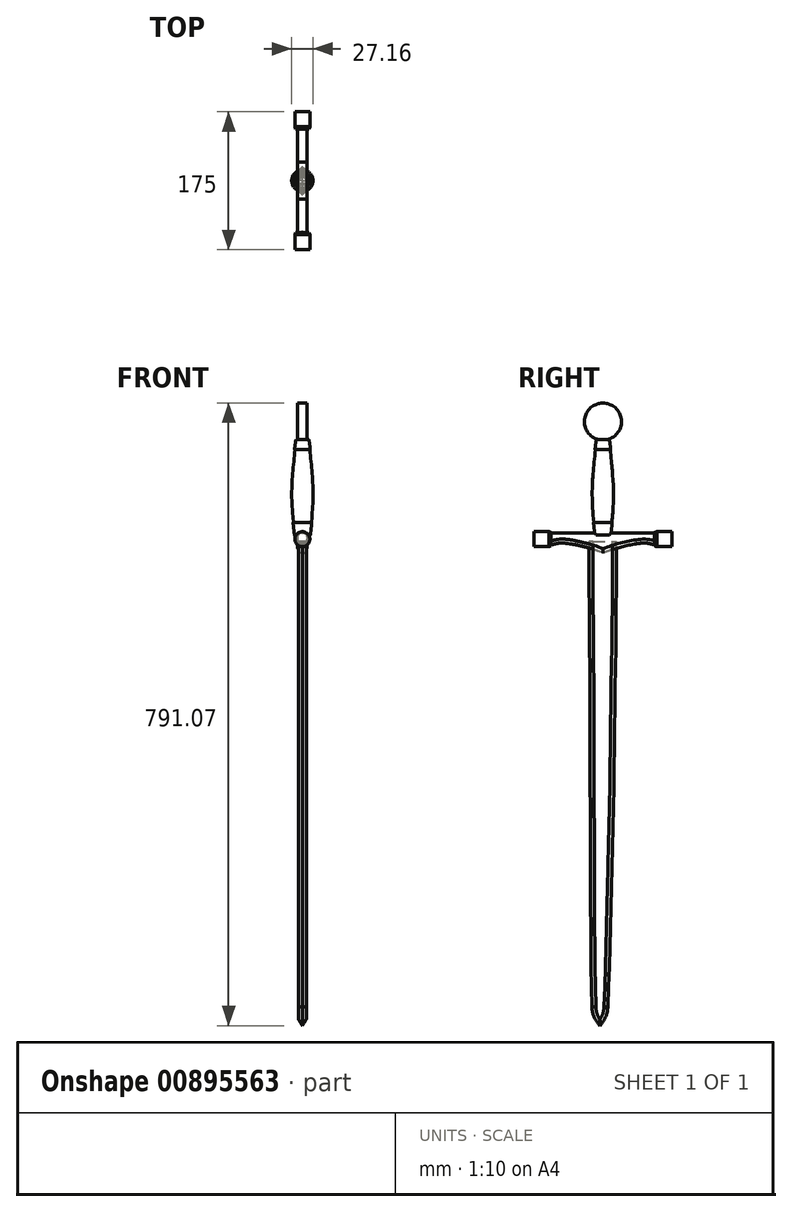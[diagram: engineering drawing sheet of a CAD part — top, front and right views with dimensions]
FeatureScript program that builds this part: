
annotation { "Feature Type Name" : "Feature", "Feature Type Description" : "" }
export const myFeature = defineFeature(function(context is Context, id is Id, definition is map)
    precondition{}
    {
        {
            var Q0;
            Q0=qCreatedBy(makeId("Right.planeOp"),FACE);
            var sketch = newSketch(context, id + "F0", { "sketchPlane" : qUnion([Q0])});
            skFitSpline(sketch, "E0", {"points": [v(15.7, 316.85) * mm, v(15.44, 255.83) * mm, v(14.96, 183.2) * mm, v(13.55, 114.23) * mm, v(12.35, 11.96) * mm, v(11.01, -48.46) * mm, v(9.54, -115.03) * mm, v(7.8, -186.55) * mm, v(6.57, -230.05) * mm, v(4.54, -274.5) * mm], "startDerivative": vector(8.51, -507.05) * mm, "endDerivative": vector(-24.21, -488.92) * mm});
            skFitSpline(sketch, "E1", {"points": [v(4.54, -274.5) * mm, v(-5.59, -298.39) * mm], "startDerivative": vector(0.63, -32.82) * mm, "endDerivative": vector(-13.34, -16.01) * mm});
            skFitSpline(sketch, "E2.MirrorCS", {"points": [v(-18.98, 316.87) * mm, v(-19.04, 251.48) * mm, v(-18.4, 181.8) * mm, v(-18.09, 112.43) * mm, v(-17.8, 12.24) * mm, v(-17.58, -48.2) * mm, v(-17.34, -114.78) * mm, v(-16.92, -186.32) * mm, v(-16.49, -229.84) * mm, v(-15.28, -274.31) * mm], "startDerivative": vector(-17.86, -506.8) * mm, "endDerivative": vector(15.2, -489.28) * mm});
            skFitSpline(sketch, "E3.MirrorCS", {"points": [v(-15.28, -274.31) * mm, v(-5.59, -298.39) * mm], "startDerivative": vector(-1.24, -32.8) * mm, "endDerivative": vector(13.04, -16.26) * mm});
            skLineSegment(sketch, "E4", {"start": v(-18.98, 316.87) * mm, "end": v(15.7, 316.85) * mm});
            skSolve(sketch);
        }
        {
            var Q0;
            Q0=qSketchRegion(id+"F0",true);
            extrude(context, id + "F1", {"entities" : qUnion([Q0]), "depth" : 10 * mm, "offsetDistance" : 25 * mm, "symmetric" : true});
        }
        {
            var Q0;
            Q0=qCreatedBy(makeId("Right.planeOp"),FACE);
            var sketch = newSketch(context, id + "F2", { "sketchPlane" : qUnion([Q0])});
            skLineSegment(sketch, "E5", {"start": v(-1.64, 330.11) * mm, "end": v(-1.64, 427.76) * mm, "construction": true});
            skLineSegment(sketch, "E6.bottom", {"start": v(85.86, 329.29) * mm, "end": v(67.01, 329.29) * mm});
            skLineSegment(sketch, "E6.top", {"start": v(85.86, 319.79) * mm, "end": v(67.01, 319.79) * mm});
            skLineSegment(sketch, "E6.left", {"start": v(85.86, 329.29) * mm, "end": v(85.86, 319.79) * mm});
            skLineSegment(sketch, "E7", {"start": v(64.02, 328.44) * mm, "end": v(64.02, 319.79) * mm});
            skLineSegment(sketch, "E8", {"start": v(67.01, 319.79) * mm, "end": v(64.02, 319.79) * mm});
            skLineSegment(sketch, "E9", {"start": v(64.02, 328.44) * mm, "end": v(67.01, 329.29) * mm});
            skLineSegment(sketch, "E10.MirrorCS", {"start": v(-67.3, 328.44) * mm, "end": v(-70.3, 329.29) * mm});
            skLineSegment(sketch, "E11.MirrorCS", {"start": v(-70.3, 319.79) * mm, "end": v(-67.3, 319.79) * mm});
            skLineSegment(sketch, "E12.MirrorCS", {"start": v(-89.14, 329.29) * mm, "end": v(-89.14, 319.79) * mm});
            skLineSegment(sketch, "E13.MirrorCS", {"start": v(-89.14, 329.29) * mm, "end": v(-70.3, 329.29) * mm});
            skLineSegment(sketch, "E14.MirrorCS", {"start": v(-67.3, 328.44) * mm, "end": v(-67.3, 319.79) * mm});
            skLineSegment(sketch, "E15.MirrorCS", {"start": v(-89.14, 319.79) * mm, "end": v(-70.3, 319.79) * mm});
            skSolve(sketch);
        }
        {
            var Q0;
            Q0=makeQuery(id+"F2.imprint","IMPRINT",FACE,{"disambiguationData":[TD([[makeQuery(id+"F2.imprint","IMPRINT",EDGE,{"derivedFrom":sQuery(id+"F2.wireOp",EDGE,"E10.MirrorCS")}),1.0]])]});
            var Q1;
            Q1=makeQuery(id+"F2.imprint","IMPRINT",FACE,{"disambiguationData":[TD([[makeQuery(id+"F2.imprint","IMPRINT",EDGE,{"derivedFrom":sQuery(id+"F2.wireOp",EDGE,"E6.bottom")}),1.0]])]});
            var Q2;
            Q2=sQuery(id+"F2.wireOp",EDGE,"E15.MirrorCS");
            revolve(context, id + "F3", {"surfaceOperationType" : NewSurfaceOperationType.NEW, "entities" : qUnion([Q0, Q1]), "axis" : qUnion([Q2]), "revolveType" : RevolveType.FULL});
        }
        {
            var Q0;
            Q0=makeQuery(id+"F1.opExtrude","CAP_EDGE",EDGE,{"disambiguationData":[OSD([sQuery(id+"F0.wireOp",EDGE,"E0")])],"isStart":false});
            var Q1;
            Q1=makeQuery(id+"F1.opExtrude","CAP_EDGE",EDGE,{"disambiguationData":[OSD([sQuery(id+"F0.wireOp",EDGE,"E1")])],"isStart":false});
            var Q2;
            Q2=makeQuery(id+"F1.opExtrude","CAP_EDGE",EDGE,{"disambiguationData":[OSD([sQuery(id+"F0.wireOp",EDGE,"E2.MirrorCS")])],"isStart":false});
            var Q3;
            Q3=makeQuery(id+"F1.opExtrude","CAP_EDGE",EDGE,{"disambiguationData":[OSD([sQuery(id+"F0.wireOp",EDGE,"E3.MirrorCS")])],"isStart":false});
            var Q4;
            Q4=makeQuery(id+"F1.opExtrude","CAP_EDGE",EDGE,{"disambiguationData":[OSD([sQuery(id+"F0.wireOp",EDGE,"E0")])],"isStart":true});
            var Q5;
            Q5=makeQuery(id+"F1.opExtrude","CAP_EDGE",EDGE,{"disambiguationData":[OSD([sQuery(id+"F0.wireOp",EDGE,"E1")])],"isStart":true});
            var Q6;
            Q6=makeQuery(id+"F1.opExtrude","CAP_EDGE",EDGE,{"disambiguationData":[OSD([sQuery(id+"F0.wireOp",EDGE,"E3.MirrorCS")])],"isStart":true});
            var Q7;
            Q7=makeQuery(id+"F1.opExtrude","CAP_EDGE",EDGE,{"disambiguationData":[OSD([sQuery(id+"F0.wireOp",EDGE,"E2.MirrorCS")])],"isStart":true});
            chamfer(context, id + "F4", {"entities" : qUnion([Q0, Q1, Q2, Q3, Q4, Q5, Q6, Q7]), "width" : 5 * mm, "tangentPropagation" : true});
        }
        {
            var Q0;
            Q0=qCreatedBy(makeId("Right.planeOp"),FACE);
            var sketch = newSketch(context, id + "F5", { "sketchPlane" : qUnion([Q0])});
            skLineSegment(sketch, "E16", {"start": v(-68.17, 327.62) * mm, "end": v(65.33, 327.62) * mm});
            skLineSegment(sketch, "E17", {"start": v(65.33, 327.62) * mm, "end": v(65.33, 312.62) * mm});
            skLineSegment(sketch, "E18", {"start": v(65.33, 312.62) * mm, "end": v(63.6, 312.62) * mm});
            skLineSegment(sketch, "E19", {"start": v(-68.17, 327.62) * mm, "end": v(-68.17, 312.62) * mm});
            skLineSegment(sketch, "E20", {"start": v(-68.17, 312.62) * mm, "end": v(-66.43, 312.62) * mm});
            skLineSegment(sketch, "E21", {"start": v(-1.42, 321.46) * mm, "end": v(-1.42, 302.29) * mm});
            skFitSpline(sketch, "E22", {"points": [v(-66.43, 312.62) * mm, v(-56.21, 314.74) * mm, v(-36.29, 312.62) * mm, v(-1.42, 302.29) * mm], "startDerivative": vector(40.4, 11.55) * mm, "endDerivative": vector(74.12, -32.6) * mm});
            skFitSpline(sketch, "E23.MirrorCS", {"points": [v(63.6, 312.62) * mm, v(53.37, 314.74) * mm, v(33.45, 312.62) * mm, v(-1.42, 302.29) * mm], "startDerivative": vector(-40.4, 11.55) * mm, "endDerivative": vector(-74.12, -32.6) * mm});
            skSolve(sketch);
        }
        {
            var Q0;
            Q0=makeQuery(id+"F5.imprint","IMPRINT",FACE,{"disambiguationData":[TD([[makeQuery(id+"F5.imprint","IMPRINT",EDGE,{"derivedFrom":sQuery(id+"F5.wireOp",EDGE,"E16")}),-1.0]])]});
            extrude(context, id + "F6", {"entities" : qUnion([Q0]), "depth" : 12 * mm, "offsetDistance" : 25 * mm, "symmetric" : true});
        }
        {
            var Q0;
            Q0=makeQuery(id+"F6.opExtrude","CAP_EDGE",EDGE,{"disambiguationData":[OSD([sQuery(id+"F5.wireOp",EDGE,"E16")])],"isStart":false});
            var Q1;
            Q1=makeQuery(id+"F6.opExtrude","CAP_EDGE",EDGE,{"disambiguationData":[OSD([sQuery(id+"F5.wireOp",EDGE,"E16")])],"isStart":true});
            var Q2;
            Q2=makeQuery(id+"F6.opExtrude","CAP_EDGE",EDGE,{"disambiguationData":[OSD([sQuery(id+"F5.wireOp",EDGE,"E23.MirrorCS")])],"isStart":true});
            var Q3;
            Q3=makeQuery(id+"F6.opExtrude","CAP_EDGE",EDGE,{"disambiguationData":[OSD([sQuery(id+"F5.wireOp",EDGE,"E22")])],"isStart":true});
            var Q4;
            Q4=makeQuery(id+"F6.opExtrude","CAP_EDGE",EDGE,{"disambiguationData":[OSD([sQuery(id+"F5.wireOp",EDGE,"E23.MirrorCS")])],"isStart":false});
            var Q5;
            Q5=makeQuery(id+"F6.opExtrude","CAP_EDGE",EDGE,{"disambiguationData":[OSD([sQuery(id+"F5.wireOp",EDGE,"E22")])],"isStart":false});
            fillet(context, id + "F7", {"entities" : qUnion([Q0, Q1, Q2, Q3, Q4, Q5]), "radius" : 5 * mm, "tangentPropagation" : true, "allowEdgeOverflow" : false});
        }
        {
            var Q0;
            Q0=qCreatedBy(makeId("Right.planeOp"),FACE);
            var sketch = newSketch(context, id + "F8", { "sketchPlane" : qUnion([Q0])});
            skLineSegment(sketch, "E24", {"start": v(6.6, 446.2) * mm, "end": v(-1.64, 446.2) * mm});
            skFitSpline(sketch, "E25", {"points": [v(6.6, 446.2) * mm, v(9.84, 418.06) * mm, v(11.75, 395.73) * mm, v(12.25, 367.67) * mm, v(9.58, 334.63) * mm, v(8.44, 324.9) * mm], "startDerivative": vector(16.88, -86.61) * mm, "endDerivative": vector(-7.07, -56.28) * mm});
            skLineSegment(sketch, "E26", {"start": v(8.44, 324.9) * mm, "end": v(-1.64, 324.9) * mm});
            skLineSegment(sketch, "E27", {"start": v(-1.64, 446.2) * mm, "end": v(-1.64, 324.9) * mm});
            skFitSpline(sketch, "E28.0", {"points": [v(6.12, 446.1) * mm, v(6.46, 444.32) * mm, v(6.97, 440.91) * mm, v(7.62, 435.52) * mm, v(8.08, 431.2) * mm, v(8.52, 426.76) * mm, v(8.94, 422.33) * mm, v(9.34, 418.06) * mm, v(9.7, 414.11) * mm, v(10.05, 410.41) * mm, v(10.37, 406.89) * mm, v(10.67, 403.47) * mm, v(10.94, 400.09) * mm, v(11.2, 396.67) * mm, v(11.42, 393.14) * mm, v(11.62, 389.48) * mm, v(11.78, 385.68) * mm, v(11.88, 381.73) * mm, v(11.93, 377.63) * mm, v(11.9, 373.37) * mm, v(11.8, 368.94) * mm, v(11.6, 364.32) * mm, v(11.33, 359.6) * mm, v(11, 354.85) * mm, v(10.49, 348.62) * mm, v(9.93, 342.74) * mm, v(9.4, 337.59) * mm, v(9.03, 334.18) * mm, v(8.7, 331.3) * mm, v(8.33, 328.05) * mm, v(8.1, 326.13) * mm, v(7.95, 324.96) * mm]});
            skLineSegment(sketch, "E29", {"start": v(9.72, 340.76) * mm, "end": v(10.22, 340.76) * mm});
            skLineSegment(sketch, "E30", {"start": v(7.8, 433.87) * mm, "end": v(8.3, 433.87) * mm});
            skLineSegment(sketch, "E31", {"start": v(9.72, 340.76) * mm, "end": v(-1.64, 340.76) * mm});
            skLineSegment(sketch, "E32", {"start": v(7.8, 433.87) * mm, "end": v(-1.64, 433.87) * mm});
            skSolve(sketch);
        }
        {
            var Q0;
            Q0=makeQuery(id+"F8.imprint","IMPRINT",FACE,{"disambiguationData":[TD([[makeQuery(id+"F8.imprint","IMPRINT",EDGE,{"derivedFrom":sQuery(id+"F8.wireOp",EDGE,"E24")}),1.0]])]});
            var Q1;
            {var subQ1=sQuery(id+"F8.wireOp",EDGE,"E26");Q1=makeQuery(id+"F8.imprint","IMPRINT",FACE,{"disambiguationData":[TD([[makeQuery(id+"F8.imprint","IMPRINT",EDGE,{"derivedFrom":subQ1}),-1.0]])]});}
            var Q2;
            Q2=sQuery(id+"F8.wireOp",EDGE,"E27");
            revolve(context, id + "F9", {"operationType" : NewBodyOperationType.ADD, "surfaceOperationType" : NewSurfaceOperationType.NEW, "entities" : qUnion([Q0, Q1]), "axis" : qUnion([Q2]), "revolveType" : RevolveType.FULL});
        }
        {
            var Q0;
            Q0=qCreatedBy(makeId("Right.planeOp"),FACE);
            var sketch = newSketch(context, id + "F10", { "sketchPlane" : qUnion([Q0])});
            skCircle(sketch, "E33", {"center": v(-1.56, 469.1) * mm, "radius": 23.58 * mm});
            skSolve(sketch);
        }
        {
            var Q0;
            Q0=makeQuery(id+"F10.imprint","IMPRINT",FACE,{"disambiguationData":[TD([[makeQuery(id+"F10.imprint","IMPRINT",EDGE,{"derivedFrom":sQuery(id+"F10.wireOp",EDGE,"E33")}),1.0]])]});
            extrude(context, id + "F11", {"entities" : qUnion([Q0]), "operationType" : NewBodyOperationType.ADD, "depth" : 12 * mm, "offsetDistance" : 25 * mm, "symmetric" : true});
        }
        {
            var Q0;
            Q0=makeQuery(id+"F8.imprint","IMPRINT",FACE,{"disambiguationData":[TD([[makeQuery(id+"F8.imprint","IMPRINT",EDGE,{"derivedFrom":sQuery(id+"F8.wireOp",EDGE,"E28.0")}),-1.0]])]});
            var Q1;
            Q1=sQuery(id+"F8.wireOp",EDGE,"E27");
            revolve(context, id + "F12", {"surfaceOperationType" : NewSurfaceOperationType.NEW, "entities" : qUnion([Q0]), "axis" : qUnion([Q1]), "revolveType" : RevolveType.FULL});
        }
    });
